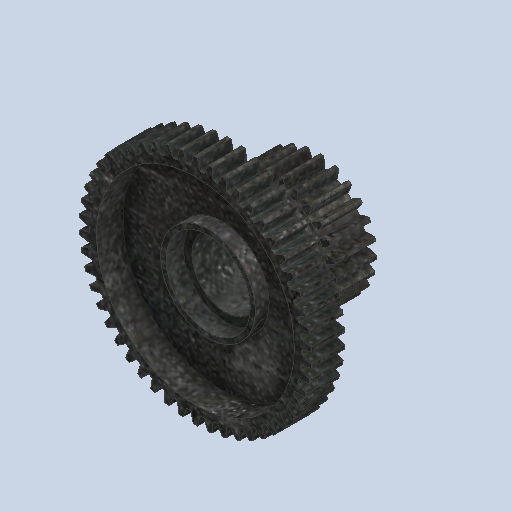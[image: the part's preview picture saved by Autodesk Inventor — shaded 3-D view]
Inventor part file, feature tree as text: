
AUTODESK INVENTOR PART (.ipt)
format: ipt  version: 2024 (Build 280153000, 153)  size: 673,280 bytes
history: native  units: in
note: dims shown in document units (in); Inventor stores cm internally (conversion verified against a paired STEP export)
features: chamfer x1
ambient origin geometry x8: Origin, YZ Plane, XZ Plane, XY Plane, X Axis, Y Axis, Z Axis, Center Point
bodies: Solid1 (feature_tree)
feature tree (1):
  chamfer  "Chamfer2"  [1 undecoded]
note: 1 required parameter value undecoded (feature->parameter linkage not recoverable at this tier; creation-order binding heuristic only, values carry confidence <= 0.55)
